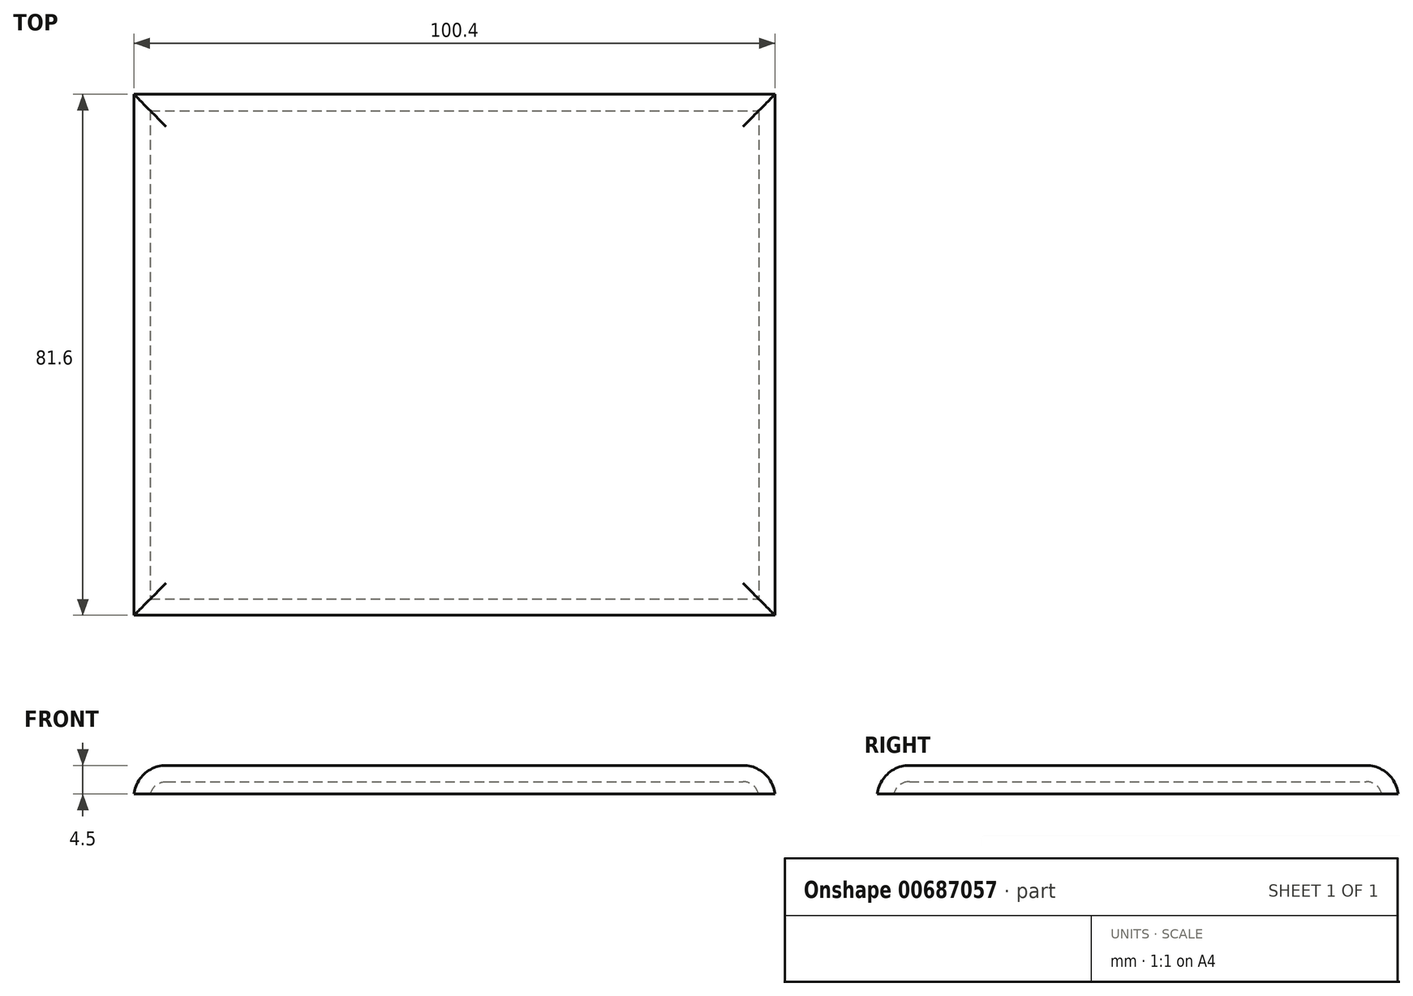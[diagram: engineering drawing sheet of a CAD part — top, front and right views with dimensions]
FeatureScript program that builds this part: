
annotation { "Feature Type Name" : "Feature", "Feature Type Description" : "" }
export const myFeature = defineFeature(function(context is Context, id is Id, definition is map)
    precondition{}
    {
        {
            var Q0;
            Q0=qCreatedBy(makeId("Top.planeOp"),FACE);
            var sketch = newSketch(context, id + "F0", { "sketchPlane" : qUnion([Q0])});
            skLineSegment(sketch, "E0.bottom", {"start": v(-51.17, 51.4) * mm, "end": v(49.23, 51.4) * mm});
            skLineSegment(sketch, "E0.top", {"start": v(-51.17, -30.2) * mm, "end": v(49.23, -30.2) * mm});
            skLineSegment(sketch, "E0.left", {"start": v(-51.17, 51.4) * mm, "end": v(-51.17, -30.2) * mm});
            skLineSegment(sketch, "E0.right", {"start": v(49.23, 51.4) * mm, "end": v(49.23, -30.2) * mm});
            skSolve(sketch);
        }
        {
            var Q0;
            Q0=makeQuery(id+"F0.imprint","IMPRINT",FACE,{"disambiguationData":[TD([[makeQuery(id+"F0.imprint","IMPRINT",EDGE,{"derivedFrom":sQuery(id+"F0.wireOp",EDGE,"E0.bottom")}),-1.0]])]});
            extrude(context, id + "F1", {"entities" : qUnion([Q0]), "depth" : 4.5 * mm, "offsetDistance" : 25.4 * mm});
        }
        {
            var Q0;
            Q0=makeQuery(id+"F1.opExtrude","CAP_FACE",FACE,{"disambiguationData":[OSD([sQuery(id+"F0.wireOp",EDGE,"E0.bottom"),sQuery(id+"F0.wireOp",EDGE,"E0.top"),sQuery(id+"F0.wireOp",EDGE,"E0.left"),sQuery(id+"F0.wireOp",EDGE,"E0.right")])],"isStart":false});
            fillet(context, id + "F2", {"entities" : qUnion([Q0]), "radius" : 5.08 * mm, "tangentPropagation" : true, "allowEdgeOverflow" : false});
        }
        {
            var Q0;
            Q0=makeQuery(id+"F1.opExtrude","CAP_FACE",FACE,{"disambiguationData":[OSD([sQuery(id+"F0.wireOp",EDGE,"E0.bottom"),sQuery(id+"F0.wireOp",EDGE,"E0.top"),sQuery(id+"F0.wireOp",EDGE,"E0.left"),sQuery(id+"F0.wireOp",EDGE,"E0.right")])],"isStart":true});
            shell(context, id + "F3", {"entities" : qUnion([Q0]), "thickness" : 2.54 * mm});
        }
    });
